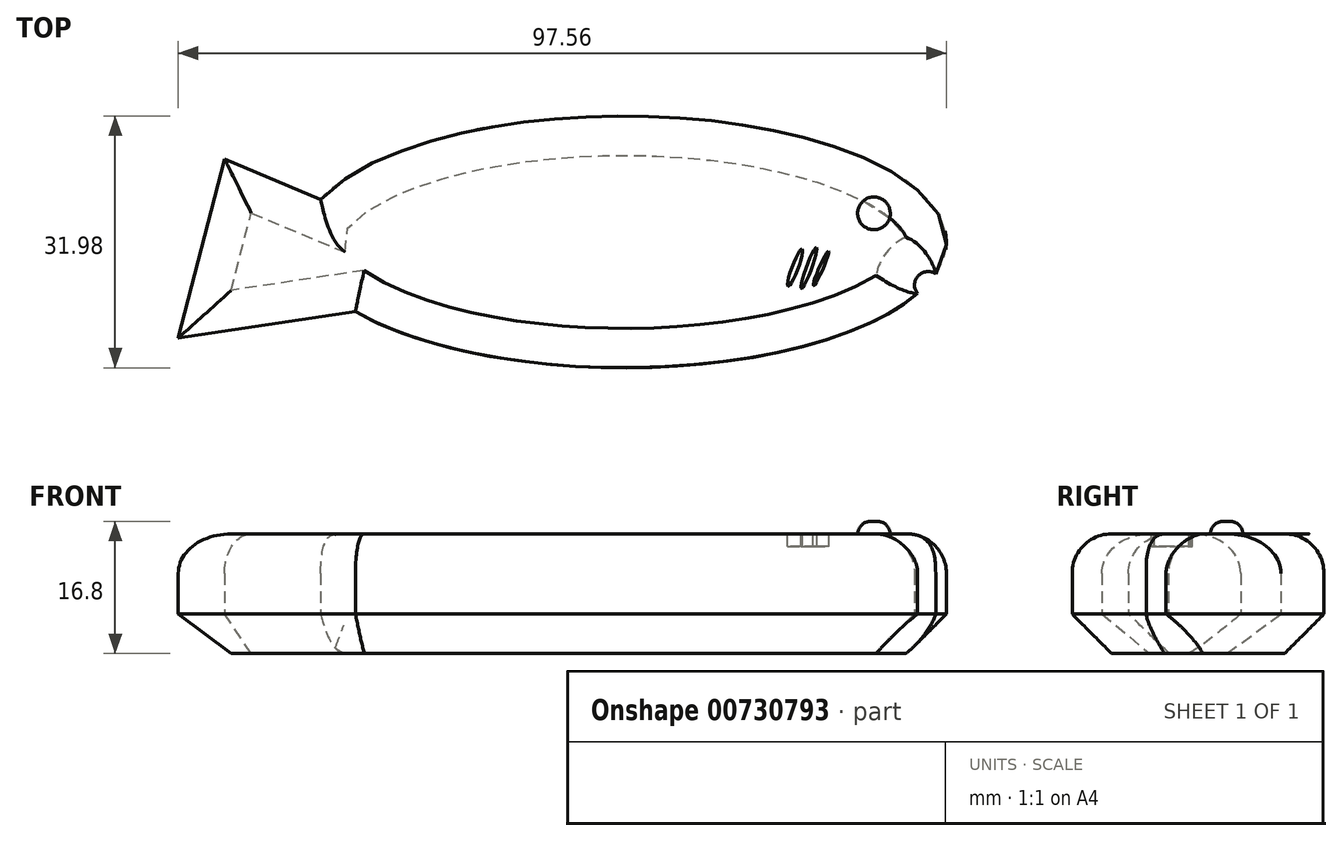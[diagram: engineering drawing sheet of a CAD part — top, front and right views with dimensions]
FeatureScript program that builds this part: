
annotation { "Feature Type Name" : "Feature", "Feature Type Description" : "" }
export const myFeature = defineFeature(function(context is Context, id is Id, definition is map)
    precondition{}
    {
        {
            var Q0;
            Q0=qCreatedBy(makeId("Top.planeOp"),FACE);
            var sketch = newSketch(context, id + "F0", { "sketchPlane" : qUnion([Q0])});
            skEllipse(sketch, "E0", {"center": v(0, 0) * mm, "majorRadius": 40.94 * mm, "minorRadius": 16 * mm, "majorAxis": v(1, 0)});
            skLineSegment(sketch, "E1", {"start": v(-38.53, 5.4) * mm, "end": v(-50.74, 10.52) * mm});
            skLineSegment(sketch, "E2", {"start": v(-50.74, 10.52) * mm, "end": v(-56.62, -12.22) * mm});
            skLineSegment(sketch, "E3", {"start": v(-56.62, -12.22) * mm, "end": v(-34.11, -8.85) * mm});
            skPoint(sketch, "E4", {"position": v(31.76, 3.62) * mm});
            skArc(sketch, "E5", {"start": v(39.6, -4.07) * mm, "mid": v(37.36, -4.33) * mm, "end": v(37.3, -6.59) * mm});
            skSolve(sketch);
        }
        {
            var Q0;
            {var subQ3=sQuery(id+"F0.wireOp",EDGE,"E5");Q0=makeQuery(id+"F0.imprint","IMPRINT",FACE,{"disambiguationData":[TD([[makeQuery(id+"F0.imprint","IMPRINT",EDGE,{"derivedFrom":subQ3}),-1.0]])]});}
            var Q1;
            {var subQ0=sQuery(id+"F0.wireOp",EDGE,"E1");Q1=makeQuery(id+"F0.imprint","IMPRINT",FACE,{"disambiguationData":[TD([[makeQuery(id+"F0.imprint","IMPRINT",EDGE,{"derivedFrom":subQ0}),1.0]])]});}
            extrude(context, id + "F1", {"entities" : qUnion([Q0, Q1]), "depth" : 15.2 * mm, "offsetDistance" : 25 * mm});
        }
        {
            var Q0;
            Q0=makeQuery(id+"F1.opExtrude","CAP_FACE",FACE,{"disambiguationData":[OSD([sQuery(id+"F0.wireOp",EDGE,"E0"),sQuery(id+"F0.wireOp",EDGE,"E1"),sQuery(id+"F0.wireOp",EDGE,"E2"),sQuery(id+"F0.wireOp",EDGE,"E3"),sQuery(id+"F0.wireOp",EDGE,"E5")])],"isStart":false});
            var sketch = newSketch(context, id + "F2", { "sketchPlane" : qUnion([Q0])});
            skCircle(sketch, "E6", {"center": v(31.76, 3.62) * mm, "radius": 2.08 * mm});
            skLineSegment(sketch, "E7", {"start": v(-20.7, -5.28) * mm, "end": v(-12.07, -5.28) * mm});
            skFitSpline(sketch, "E8", {"points": [v(-22.29, -0.93) * mm, v(-17.5, -0.8) * mm, v(-11.12, -2.35) * mm, v(-11.2, -4.83) * mm, v(-12.9, -5.72) * mm, v(-22.29, -4.88) * mm, v(-25.84, -0.8) * mm, v(-22.29, -0.93) * mm]});
            skEllipse(sketch, "E9", {"center": v(25.03, -3.36) * mm, "majorRadius": 2.4 * mm, "minorRadius": 0.25 * mm, "majorAxis": v(0.4, 0.92)});
            skEllipse(sketch, "E10", {"center": v(23.5, -3.31) * mm, "majorRadius": 2.76 * mm, "minorRadius": 0.35 * mm, "majorAxis": v(0.35, 0.94)});
            skEllipse(sketch, "E11", {"center": v(21.74, -3.26) * mm, "majorRadius": 2.52 * mm, "minorRadius": 0.39 * mm, "majorAxis": v(0.35, 0.94)});
            skPoint(sketch, "E11.centerSnap0", {"position": v(24.8, -3.26) * mm});
            skSolve(sketch);
        }
        {
            var Q0;
            Q0=makeQuery(id+"F1.opExtrude","CAP_FACE",FACE,{"disambiguationData":[OSD([sQuery(id+"F0.wireOp",EDGE,"E0"),sQuery(id+"F0.wireOp",EDGE,"E1"),sQuery(id+"F0.wireOp",EDGE,"E2"),sQuery(id+"F0.wireOp",EDGE,"E3"),sQuery(id+"F0.wireOp",EDGE,"E5")])],"isStart":true});
            chamfer(context, id + "F3", {"entities" : qUnion([Q0]), "width" : 5 * mm, "tangentPropagation" : true});
        }
        {
            var Q0;
            {var subQ0=sQuery(id+"F0.wireOp",EDGE,"E0");Q0=makeQuery(id+"F1.opExtrude","CAP_EDGE",EDGE,{"disambiguationData":[OSD([subQ0]),TDD([makeQuery(id+"F0.imprint","IMPRINT",EDGE,{"disambiguationData":[TD([[makeQuery(id+"F0.imprint","INTERSECT",VERTEX,{"derivedFrom":[subQ0,sQuery(id+"F0.wireOp",EDGE,"E3")]}),-1.0]])],"derivedFrom":subQ0})])],"isStart":false});}
            var Q1;
            Q1=makeQuery(id+"F1.opExtrude","CAP_EDGE",EDGE,{"disambiguationData":[OSD([sQuery(id+"F0.wireOp",EDGE,"E3")])],"isStart":false});
            var Q2;
            Q2=makeQuery(id+"F1.opExtrude","CAP_EDGE",EDGE,{"disambiguationData":[OSD([sQuery(id+"F0.wireOp",EDGE,"E2")])],"isStart":false});
            var Q3;
            Q3=makeQuery(id+"F1.opExtrude","CAP_EDGE",EDGE,{"disambiguationData":[OSD([sQuery(id+"F0.wireOp",EDGE,"E1")])],"isStart":false});
            var Q4;
            {var subQ0=sQuery(id+"F0.wireOp",EDGE,"E0");Q4=makeQuery(id+"F1.opExtrude","CAP_EDGE",EDGE,{"disambiguationData":[OSD([subQ0]),TDD([makeQuery(id+"F0.imprint","IMPRINT",EDGE,{"disambiguationData":[TD([[makeQuery(id+"F0.imprint","INTERSECT",VERTEX,{"derivedFrom":[subQ0,sQuery(id+"F0.wireOp",EDGE,"E1")]}),1.0]])],"derivedFrom":subQ0})])],"isStart":false});}
            var Q5;
            Q5=makeQuery(id+"F1.opExtrude","CAP_EDGE",EDGE,{"disambiguationData":[OSD([sQuery(id+"F0.wireOp",EDGE,"E5")])],"isStart":false});
            fillet(context, id + "F4", {"entities" : qUnion([Q0, Q1, Q2, Q3, Q4, Q5]), "radius" : 5 * mm, "tangentPropagation" : true, "allowEdgeOverflow" : false});
        }
        {
            var Q0;
            Q0=makeQuery(id+"F2.imprint","IMPRINT",FACE,{"disambiguationData":[TD([[makeQuery(id+"F2.imprint","IMPRINT",EDGE,{"derivedFrom":sQuery(id+"F2.wireOp",EDGE,"E6")}),1.0]])]});
            extrude(context, id + "F5", {"entities" : qUnion([Q0]), "operationType" : NewBodyOperationType.ADD, "depth" : 1.6 * mm, "offsetDistance" : 25 * mm});
        }
        {
            var Q0;
            Q0=makeQuery(id+"F5.opExtrude","CAP_FACE",FACE,{"disambiguationData":[OSD([sQuery(id+"F2.wireOp",EDGE,"E6")])],"isStart":false});
            fillet(context, id + "F6", {"entities" : qUnion([Q0]), "radius" : 1.69 * mm, "tangentPropagation" : true, "allowEdgeOverflow" : false});
        }
        {
            var Q0;
            Q0=makeQuery(id+"F2.imprint","IMPRINT",FACE,{"disambiguationData":[TD([[makeQuery(id+"F2.imprint","IMPRINT",EDGE,{"derivedFrom":sQuery(id+"F2.wireOp",EDGE,"E11")}),1.0]])]});
            var Q1;
            Q1=makeQuery(id+"F2.imprint","IMPRINT",FACE,{"disambiguationData":[TD([[makeQuery(id+"F2.imprint","IMPRINT",EDGE,{"derivedFrom":sQuery(id+"F2.wireOp",EDGE,"E10")}),1.0]])]});
            var Q2;
            Q2=makeQuery(id+"F2.imprint","IMPRINT",FACE,{"disambiguationData":[TD([[makeQuery(id+"F2.imprint","IMPRINT",EDGE,{"derivedFrom":sQuery(id+"F2.wireOp",EDGE,"E9")}),1.0]])]});
            extrude(context, id + "F7", {"entities" : qUnion([Q0, Q1, Q2]), "operationType" : NewBodyOperationType.REMOVE, "oppositeDirection" : true, "depth" : 1.6 * mm, "offsetDistance" : 25 * mm});
        }
    });
